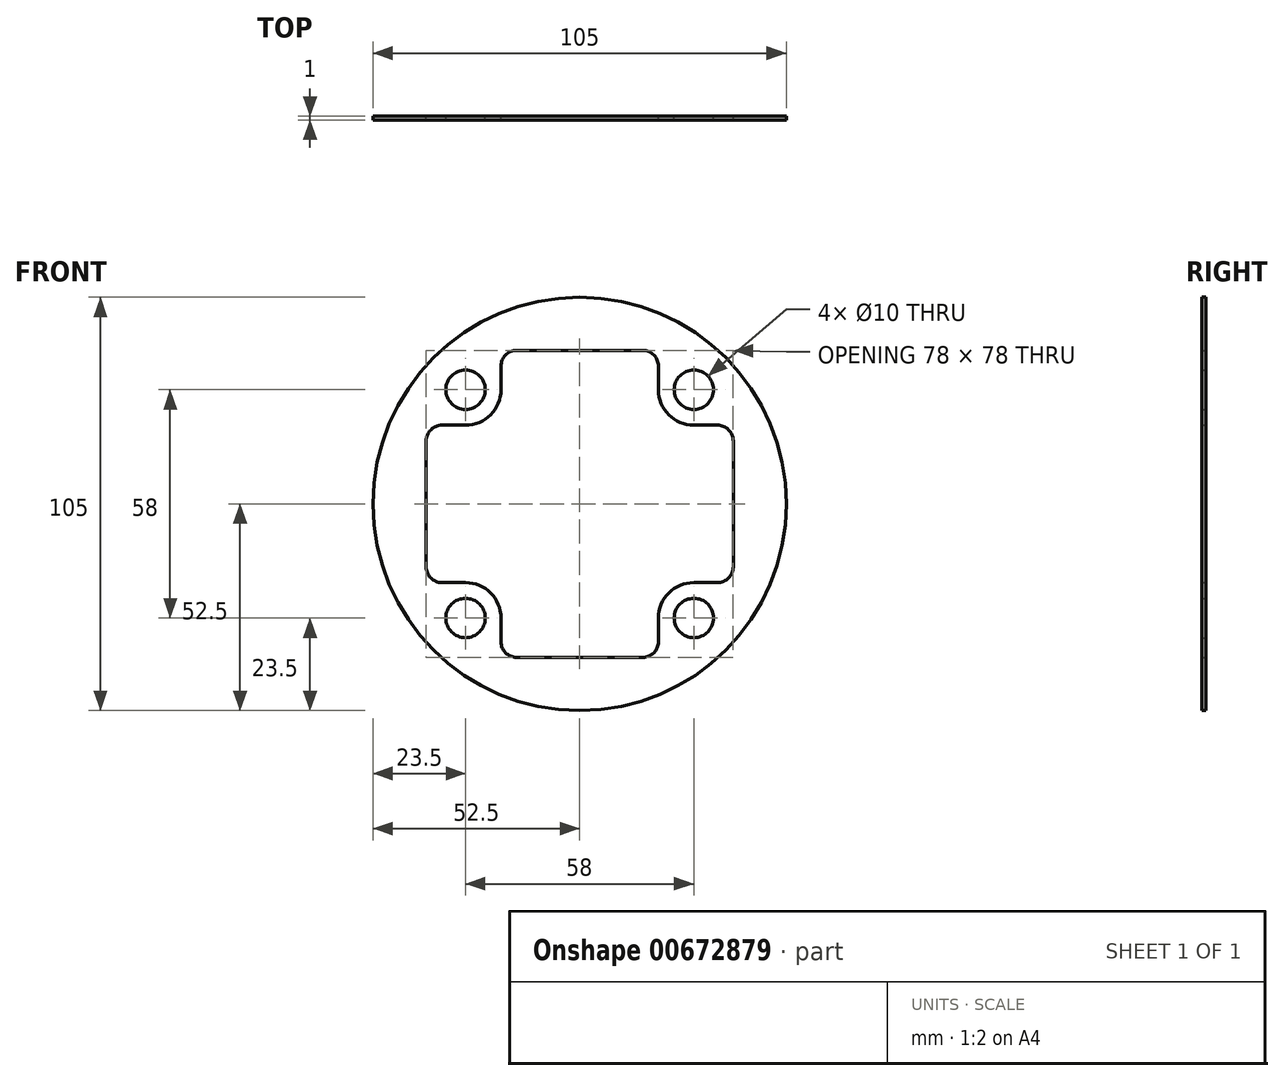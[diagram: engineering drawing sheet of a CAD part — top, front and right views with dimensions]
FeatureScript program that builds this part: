
annotation { "Feature Type Name" : "Feature", "Feature Type Description" : "" }
export const myFeature = defineFeature(function(context is Context, id is Id, definition is map)
    precondition{}
    {
        {
            var Q0;
            Q0=qCreatedBy(makeId("Front.planeOp"),FACE);
            var sketch = newSketch(context, id + "F0", { "sketchPlane" : qUnion([Q0])});
            skCircle(sketch, "E0", {"center": v(0, 0) * mm, "radius": 52.5 * mm});
            skLineSegment(sketch, "E1.top", {"start": v(-35, 20) * mm, "end": v(-29, 20) * mm});
            skLineSegment(sketch, "E1.right", {"start": v(-20, 35) * mm, "end": v(-20, 29) * mm});
            skLineSegment(sketch, "E2.top", {"start": v(35, 20) * mm, "end": v(29, 20) * mm});
            skLineSegment(sketch, "E2.right", {"start": v(20, 35) * mm, "end": v(20, 29) * mm});
            skLineSegment(sketch, "E3.top", {"start": v(-35, -20) * mm, "end": v(-29, -20) * mm});
            skLineSegment(sketch, "E3.right", {"start": v(-20, -35) * mm, "end": v(-20, -29) * mm});
            skLineSegment(sketch, "E4.top", {"start": v(35, -20) * mm, "end": v(29, -20) * mm});
            skLineSegment(sketch, "E4.right", {"start": v(20, -35) * mm, "end": v(20, -29) * mm});
            skLineSegment(sketch, "E5.trimOffspring", {"start": v(-39, 16) * mm, "end": v(-39, -16) * mm});
            skLineSegment(sketch, "E6.trimOffspring", {"start": v(-16, 39) * mm, "end": v(16, 39) * mm});
            skLineSegment(sketch, "E7.trimOffspring", {"start": v(39, 16) * mm, "end": v(39, -16) * mm});
            skLineSegment(sketch, "E8.trimOffspring", {"start": v(-16, -39) * mm, "end": v(16, -39) * mm});
            skCircle(sketch, "E9", {"center": v(-29, 29) * mm, "radius": 5 * mm});
            skCircle(sketch, "E10", {"center": v(29, 29) * mm, "radius": 5 * mm});
            skCircle(sketch, "E11", {"center": v(29, -29) * mm, "radius": 5 * mm});
            skCircle(sketch, "E12", {"center": v(-29, -29) * mm, "radius": 5 * mm});
            skPoint(sketch, "E13.visualSharp", {"position": v(-20, 20) * mm});
            skArc(sketch, "E13.filletArc", {"start": v(-29, 20) * mm, "mid": v(-22.64, 22.64) * mm, "end": v(-20, 29) * mm});
            skPoint(sketch, "E14.visualSharp", {"position": v(20, 20) * mm});
            skArc(sketch, "E14.filletArc", {"start": v(20, 29) * mm, "mid": v(22.64, 22.64) * mm, "end": v(29, 20) * mm});
            skPoint(sketch, "E15.visualSharp", {"position": v(20, -20) * mm});
            skArc(sketch, "E15.filletArc", {"start": v(29, -20) * mm, "mid": v(22.64, -22.64) * mm, "end": v(20, -29) * mm});
            skPoint(sketch, "E16.visualSharp", {"position": v(-20, -20) * mm});
            skArc(sketch, "E16.filletArc", {"start": v(-20, -29) * mm, "mid": v(-22.64, -22.64) * mm, "end": v(-29, -20) * mm});
            skPoint(sketch, "E17.visualSharp", {"position": v(-39, -20) * mm});
            skArc(sketch, "E17.filletArc", {"start": v(-39, -16) * mm, "mid": v(-37.83, -18.83) * mm, "end": v(-35, -20) * mm});
            skPoint(sketch, "E18.visualSharp", {"position": v(-39, 20) * mm});
            skArc(sketch, "E18.filletArc", {"start": v(-35, 20) * mm, "mid": v(-37.83, 18.83) * mm, "end": v(-39, 16) * mm});
            skPoint(sketch, "E19.visualSharp", {"position": v(-20, 39) * mm});
            skArc(sketch, "E19.filletArc", {"start": v(-16, 39) * mm, "mid": v(-18.83, 37.83) * mm, "end": v(-20, 35) * mm});
            skPoint(sketch, "E20.visualSharp", {"position": v(20, 39) * mm});
            skArc(sketch, "E20.filletArc", {"start": v(20, 35) * mm, "mid": v(18.83, 37.83) * mm, "end": v(16, 39) * mm});
            skPoint(sketch, "E21.visualSharp", {"position": v(39, 20) * mm});
            skArc(sketch, "E21.filletArc", {"start": v(39, 16) * mm, "mid": v(37.83, 18.83) * mm, "end": v(35, 20) * mm});
            skPoint(sketch, "E22.visualSharp", {"position": v(39, -20) * mm});
            skArc(sketch, "E22.filletArc", {"start": v(35, -20) * mm, "mid": v(37.83, -18.83) * mm, "end": v(39, -16) * mm});
            skPoint(sketch, "E23.visualSharp", {"position": v(20, -39) * mm});
            skArc(sketch, "E23.filletArc", {"start": v(16, -39) * mm, "mid": v(18.83, -37.83) * mm, "end": v(20, -35) * mm});
            skPoint(sketch, "E24.visualSharp", {"position": v(-20, -39) * mm});
            skArc(sketch, "E24.filletArc", {"start": v(-20, -35) * mm, "mid": v(-18.83, -37.83) * mm, "end": v(-16, -39) * mm});
            skSolve(sketch);
        }
        {
            var Q0;
            Q0=makeQuery(id+"F0.imprint","IMPRINT",FACE,{"disambiguationData":[TD([[makeQuery(id+"F0.imprint","IMPRINT",EDGE,{"derivedFrom":sQuery(id+"F0.wireOp",EDGE,"E0")}),1.0]])]});
            extrude(context, id + "F1", {"entities" : qUnion([Q0]), "depth" : 1 * mm, "offsetDistance" : 25 * mm});
        }
    });
